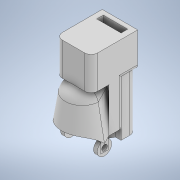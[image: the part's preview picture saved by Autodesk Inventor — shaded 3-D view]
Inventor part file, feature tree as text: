
AUTODESK INVENTOR PART (.ipt)
format: ipt  version: 2022 (Build 260153000, 153)  size: 441,344 bytes
history: native  units: mm
features: sketch x16, extrude x10, other x5, fillet x4, loft x1, shell x1, projected_geometry x1
ambient origin geometry x8: Origin, YZ Plane, XZ Plane, XY Plane, X Axis, Y Axis, Z Axis, Center Point
bodies: Body1 (feature_tree)
feature tree (38):
  sketch  "스케치2"
  other  "작업 평면2"
  sketch  "스케치3"
  other  "작업 평면4"
  loft  "로프트1"
  fillet  "모깎기1"  Radius=5.0mm
  sketch  "스케치5"
  extrude  "돌출2"  Depth=20.0mm
  other  "작업 평면5"
  sketch  "스케치7"
  sketch  "스케치11"
  shell  "쉘2"  Thickness=-20.0mm
  sketch  "스케치16"
  extrude  "돌출10"  TaperAngle=0.0deg  [1 undecoded]
  sketch  "스케치20"
  extrude  "돌출13"  TaperAngle=0.0deg  [1 undecoded]
  sketch  "스케치22"
  other  "작업 평면8"
  extrude  "돌출14"  TaperAngle=0.0deg  [1 undecoded]
  extrude  "돌출15"  Depth=5.5mm
  extrude  "돌출16"  Depth=43.5mm TaperAngle=0.0deg
  sketch  "스케치27"
  fillet  "모깎기2"  [1 undecoded]
  sketch  "스케치28"
  fillet  "모깎기3"  Radius=5.0mm
  fillet  "모깎기4"  Radius=5.0mm
  extrude  "돌출17"  Depth=3.0mm
  extrude  "돌출18"  Depth=5.0mm TaperAngle=0.0deg
  extrude  "돌출19"  Depth=2.5mm
  extrude  "돌출20"  Depth=2.5mm
  other  "작업 평면3"
  sketch  "스케치4"
  sketch  "스케치6"
  sketch  "스케치21"
  sketch  "스케치23"
  sketch  "스케치25"
  sketch  "스케치26"
  projected_geometry  "투영된 루프2"
note: 4 required parameter values undecoded (feature->parameter linkage not recoverable at this tier; creation-order binding heuristic only, values carry confidence <= 0.55)
